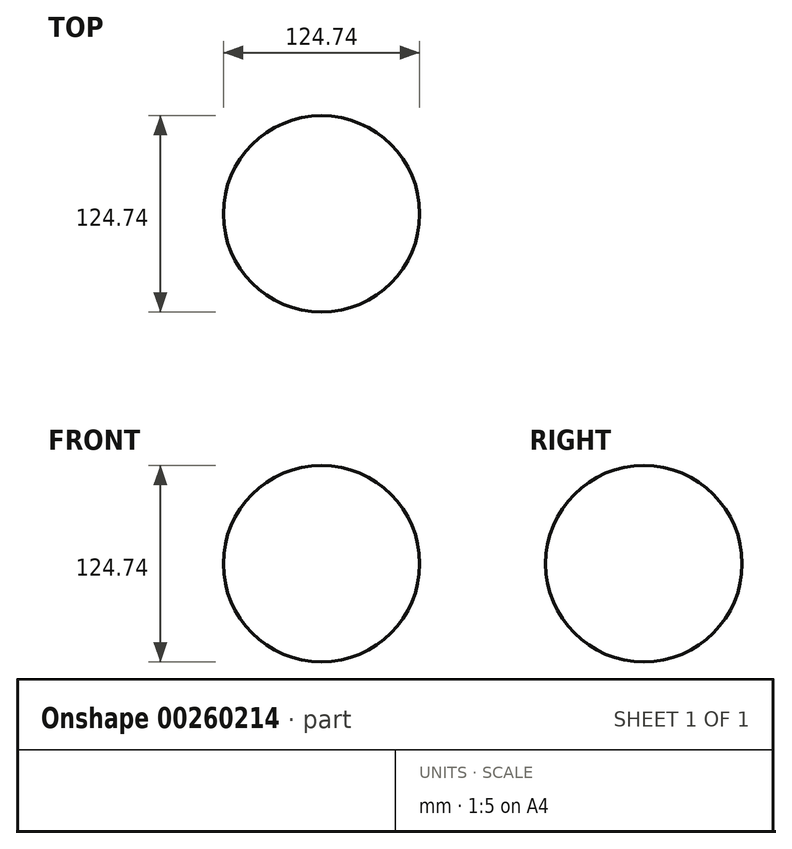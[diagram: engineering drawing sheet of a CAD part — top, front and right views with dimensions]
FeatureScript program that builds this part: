
annotation { "Feature Type Name" : "Feature", "Feature Type Description" : "" }
export const myFeature = defineFeature(function(context is Context, id is Id, definition is map)
    precondition{}
    {
        {
            var Q0;
            Q0=qCreatedBy(makeId("Front.planeOp"),FACE);
            var sketch = newSketch(context, id + "F0", { "sketchPlane" : qUnion([Q0])});
            skLineSegment(sketch, "E0", {"start": v(0, 75.53) * mm, "end": v(0, -76.32) * mm, "construction": true});
            skArc(sketch, "E1", {"start": v(0, 62.37) * mm, "mid": v(-62.37, 0) * mm, "end": v(0, -62.37) * mm});
            skLineSegment(sketch, "E2", {"start": v(0, 62.37) * mm, "end": v(0, -62.37) * mm});
            skSolve(sketch);
        }
        {
            var Q0;
            Q0 = qSketchRegion(id + "F0", true);
            var Q1;
            Q1=sQuery(id+"F0.wireOp",EDGE,"E0");
            revolve(context, id + "F1", {"entities" : qUnion([Q0]), "axis" : qUnion([Q1]), "revolveType" : RevolveType.FULL});
        }
    });
